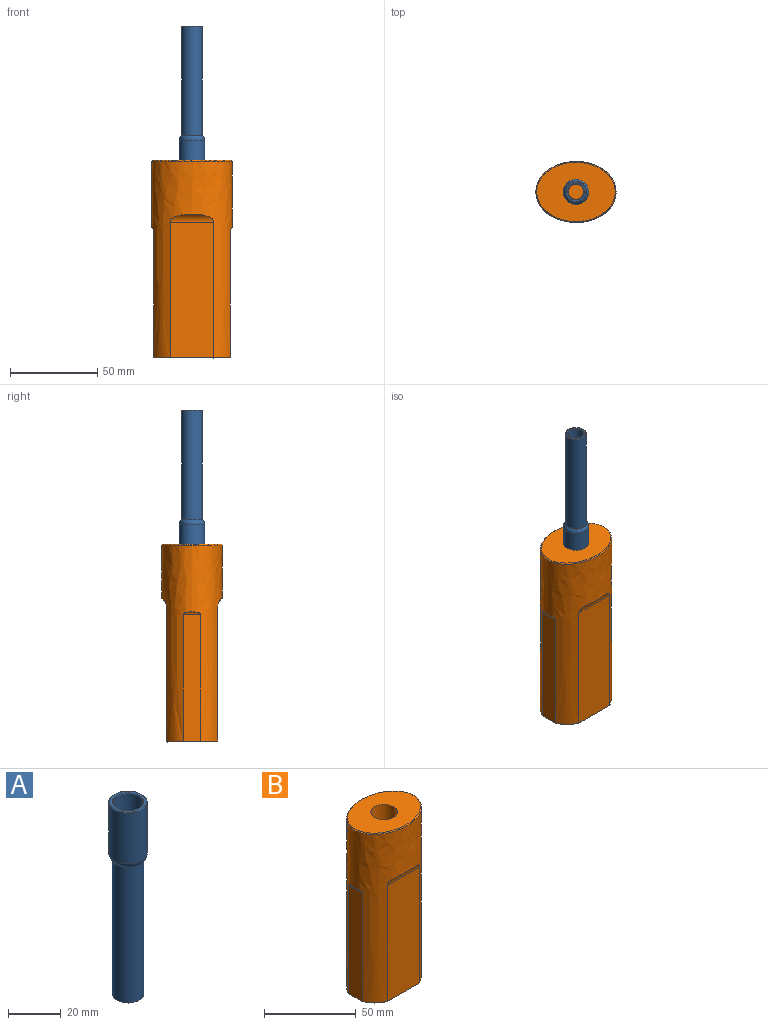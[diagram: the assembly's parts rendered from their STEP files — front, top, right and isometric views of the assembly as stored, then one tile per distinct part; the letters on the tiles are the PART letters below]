
ASSEMBLY  parts=2 mates=1
PART A: 13 faces, bbox 15.7x15.7x89 mm
  f0: cylinder r=4.4mm len=62.7mm, axis (0,0,-1), area 1733.4mm2, adj f7,f10
  f1: cylinder r=6mm len=62.55mm, axis (0,0,-1), area 2358.1mm2, adj f11,f12
  f2: plane 11.4x11.4mm, normal (0,0,-1), area 32.7mm2, adj f10,f11
  f3: cylinder r=7.25mm len=23.26mm, axis (0,0,-1), area 1059.7mm2, adj f6,f8
  f4: cylinder r=5.65mm len=23.26mm, axis (0,0,-1), area 825.8mm2, adj f7,f9
  f5: plane 13.9x13.9mm, normal (0,0,1), area 40.5mm2, adj f8,f9
  f6: torus R=4.25mm, axis (0,0,-1), area 116.5mm2, adj f3,f12
  f7: torus R=2.65mm, axis (0,0,-1), area 93.3mm2, adj f0,f4
  f8: torus R=6.95mm, axis (0,0,1), area 21.1mm2, adj f3,f5
  f9: torus R=5.95mm, axis (0,0,1), area 17.1mm2, adj f4,f5
  f10: torus R=4.7mm, axis (0,0,1), area 13.4mm2, adj f0,f2
  f11: torus R=5.7mm, axis (0,0,1), area 17.4mm2, adj f1,f2
  f12: torus R=6.3mm, axis (0,0,1), area 10.3mm2, adj f1,f6
PART B: 22 faces, bbox 57x43x121.5 mm
  f0: extruded ~112.5x46mm, area 8701.9mm2, adj f5,f6,f7,f8,f9,f10,f11,f12
  f1: plane 43.18x28.68mm, normal (0,0,-1), area 1096.5mm2, adj f13,f14,f15,f16,f17,f18,f19,f20
  f2: plane 45.24x34.24mm, normal (0,0,1), area 1034.2mm2, adj f3,f21
  f3: cylinder r=7.25mm len=18mm, axis (0,0,1), area 820mm2, adj f2,f4
  f4: plane 14.5x14.5mm, normal (0,0,1), area 165.1mm2, adj f3
  f5: plane 77.5x24.75mm, normal (0,1,0), area 1918.5mm2, adj f0,f9,f18
  f6: plane 80.5x18.21mm, normal (1,0,0), area 740.1mm2, adj f0,f12,f14
  f7: plane 77.5x24.75mm, normal (0,-1,0), area 1918.5mm2, adj f0,f10,f15
  f8: plane 72.5x10.21mm, normal (-1,0,0), area 740.1mm2, adj f0,f11,f19
  f9: cylinder r=5mm len=24.75mm, axis (1,0,0), area 107mm2, adj f0,f5
  f10: cylinder r=5mm len=24.75mm, axis (1,0,0), area 107mm2, adj f0,f7
  f11: cylinder r=2mm len=10.21mm, axis (0,1,0), area 10.7mm2, adj f0,f8
  f12: cylinder r=2mm len=10.21mm, axis (0,1,0), area 0mm2, adj f0,f6
  f13: bspline ~10.76x10.7mm, area 9.6mm2, adj f0,f1,f14,f15
  f14: plane 10.21x0.5mm, normal (0.71,0,-0.71), area 7.1mm2, adj f1,f6,f13,f16
  f15: plane 24.76x0.5mm, normal (0,-0.71,-0.71), area 17.4mm2, adj f1,f7,f13,f17
  f16: bspline ~9.84x9.83mm, area 9.6mm2, adj f0,f1,f14,f18
  f17: bspline ~9.84x9.83mm, area 9.6mm2, adj f0,f1,f15,f19
  f18: plane 24.76x0.5mm, normal (0,0.71,-0.71), area 17.4mm2, adj f1,f5,f16,f20
  f19: plane 10.21x0.5mm, normal (-0.71,0,-0.71), area 7.1mm2, adj f1,f8,f17,f20
  f20: bspline ~10.76x10.7mm, area 9.6mm2, adj f0,f1,f18,f19
  f21: bspline ~46x35mm, area 89.3mm2, adj f0,f2
PLACE A rot(axis=(0,-1,0),180deg) t=(-3.84,40.3,184.23)mm
PLACE B t=(-3.84,40.3,-6.34)mm fixed
MATE slider A.f3 <-> B.f3  axis (0,0,1) through (-3.84,40.3,107.16)mm
